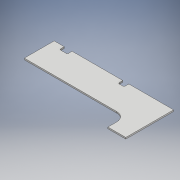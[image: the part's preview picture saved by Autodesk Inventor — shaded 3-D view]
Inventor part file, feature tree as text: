
AUTODESK INVENTOR PART (.ipt)
format: ipt  version: 2018 (Build 220112000, 112)  size: 130,560 bytes
history: native  units: mm
features: extrude x1, sketch x1
ambient origin geometry x8: Origin, YZ Plane, XZ Plane, XY Plane, X Axis, Y Axis, Z Axis, Center Point
bodies: Solid1 (feature_tree)
feature tree (2):
  extrude  "Extrusion1"  Depth=500.0mm
  sketch  "Sketch1"  dims[d2=2000.0mm d3=500.0mm d4=300.0mm d5=300.0mm d6=150.0mm d7=1550.0mm d8=150.0mm d11=80.0mm d12=100.0mm d13=170.0mm d14=80.0mm d15=130.0mm d16=850.0mm d18=20.0mm d19=20.0mm d20=20.0mm d21=20.0mm d22=25.0mm d23=0.0mm]
